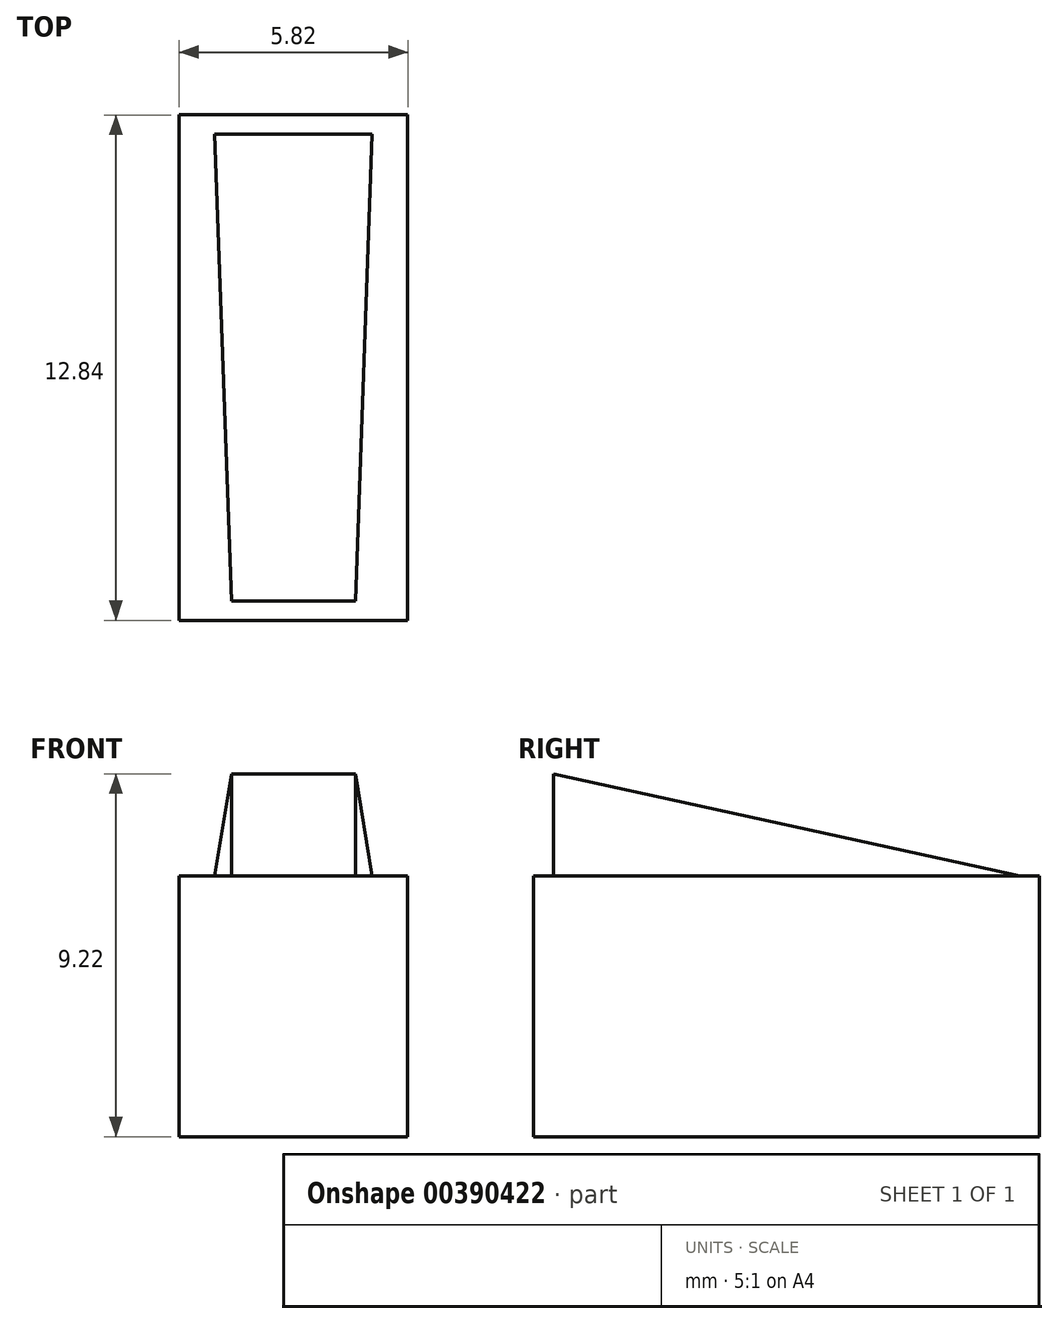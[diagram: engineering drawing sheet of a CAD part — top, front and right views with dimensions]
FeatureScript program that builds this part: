
annotation { "Feature Type Name" : "Feature", "Feature Type Description" : "" }
export const myFeature = defineFeature(function(context is Context, id is Id, definition is map)
    precondition{}
    {
        {
            assignVariable(context, id + "F0", {"name" : "height", "anyValue" : 12.85});
        }
        {
            assignVariable(context, id + "F1", {"name" : "depth", "anyValue" : 6.62});
        }
        {
            var Q0;
            Q0=qCreatedBy(makeId("Top.planeOp"),FACE);
            var sketch = newSketch(context, id + "F2", { "sketchPlane" : qUnion([Q0])});
            skLineSegment(sketch, "E0.bottom", {"start": v(-2.9, 6.42) * mm, "end": v(2.9, 6.42) * mm});
            skLineSegment(sketch, "E0.top", {"start": v(-2.9, -6.43) * mm, "end": v(2.9, -6.43) * mm});
            skLineSegment(sketch, "E0.left", {"start": v(-2.9, 6.42) * mm, "end": v(-2.9, -6.43) * mm});
            skLineSegment(sketch, "E0.right", {"start": v(2.9, 6.42) * mm, "end": v(2.9, -6.43) * mm});
            skPoint(sketch, "E0.middle", {"position": v(0, 0) * mm});
            skSolve(sketch);
        }
        {
            var Q0;
            Q0=makeQuery(id+"F2.imprint","IMPRINT",FACE,{"disambiguationData":[TD([[makeQuery(id+"F2.imprint","IMPRINT",EDGE,{"derivedFrom":sQuery(id+"F2.wireOp",EDGE,"E0.bottom")}),-1.0]])]});
            extrude(context, id + "F3", {"entities" : qUnion([Q0]), "depth" : (getVariable(context, 'depth')) * mm});
        }
        {
            var Q0;
            Q0=makeQuery(id+"F3.opExtrude","CAP_FACE",FACE,{"disambiguationData":[OSD([sQuery(id+"F2.wireOp",EDGE,"E0.bottom"),sQuery(id+"F2.wireOp",EDGE,"E0.top"),sQuery(id+"F2.wireOp",EDGE,"E0.left"),sQuery(id+"F2.wireOp",EDGE,"E0.right")])],"isStart":false});
            var sketch = newSketch(context, id + "F4", { "sketchPlane" : qUnion([Q0])});
            skLineSegment(sketch, "E1.bottom", {"start": v(-2, 5.92) * mm, "end": v(2, 5.92) * mm});
            skLineSegment(sketch, "E1.top", {"start": v(-1.57, -5.93) * mm, "end": v(1.58, -5.93) * mm});
            skLineSegment(sketch, "E1.left", {"start": v(-2, 5.93) * mm, "end": v(-1.57, -5.93) * mm});
            skLineSegment(sketch, "E1.right", {"start": v(2, 5.93) * mm, "end": v(1.58, -5.93) * mm});
            skPoint(sketch, "E1.middle", {"position": v(0, 0) * mm});
            skPoint(sketch, "E2", {"position": v(0, 6.42) * mm});
            skPoint(sketch, "E3", {"position": v(0, -6.43) * mm});
            skPoint(sketch, "E4", {"position": v(0, 5.92) * mm});
            skPoint(sketch, "E5", {"position": v(0, -5.93) * mm});
            skSolve(sketch);
        }
        {
            assignVariable(context, id + "F5", {"name" : "tab_height", "anyValue" : 2.6});
        }
        {
            var Q0;
            Q0=makeQuery(id+"F4.imprint","IMPRINT",FACE,{"disambiguationData":[TD([[makeQuery(id+"F4.imprint","IMPRINT",EDGE,{"derivedFrom":sQuery(id+"F4.wireOp",EDGE,"E1.bottom")}),-1.0]])]});
            extrude(context, id + "F6", {"entities" : qUnion([Q0]), "operationType" : NewBodyOperationType.ADD, "depth" : (getVariable(context, 'tab_height')) * mm});
        }
        {
            var Q0;
            Q0=makeQuery(id+"F6.opExtrude","CAP_EDGE",EDGE,{"disambiguationData":[OSD([sQuery(id+"F4.wireOp",EDGE,"E1.bottom")])],"isStart":false});
            chamfer(context, id + "F7", {"entities" : qUnion([Q0]), "chamferType" : ChamferType.TWO_OFFSETS, "width1" : (getVariable(context, 'tab_height')) * mm, "oppositeDirection" : false, "width2" : (getVariable(context, 'height') - 1) * mm, "tangentPropagation" : true});
        }
    });
